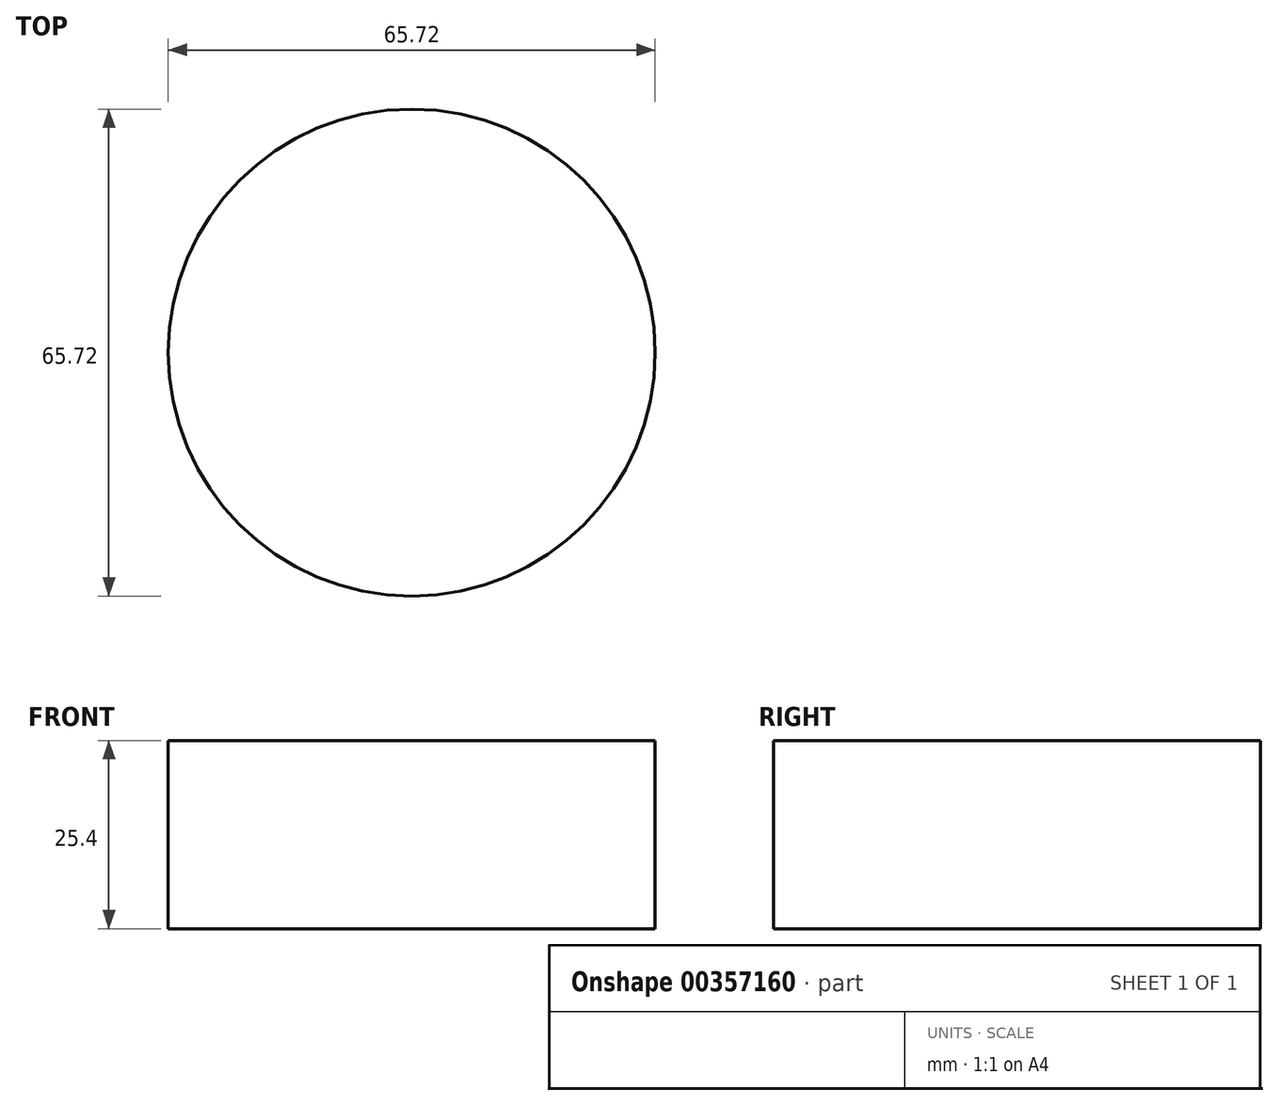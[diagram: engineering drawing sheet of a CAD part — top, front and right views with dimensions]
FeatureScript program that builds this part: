
annotation { "Feature Type Name" : "Feature", "Feature Type Description" : "" }
export const myFeature = defineFeature(function(context is Context, id is Id, definition is map)
    precondition{}
    {
        {
            var Q0;
            Q0=qCreatedBy(makeId("Top.planeOp"),FACE);
            var sketch = newSketch(context, id + "F0", { "sketchPlane" : qUnion([Q0])});
            skCircle(sketch, "E0", {"center": v(0, 0) * mm, "radius": 32.86 * mm});
            skSolve(sketch);
        }
        {
            var Q0;
            Q0 = qSketchRegion(id + "F0", true);
            extrude(context, id + "F1", {"entities" : qUnion([Q0]), "depth" : 25.4 * mm, "offsetDistance" : 25.4 * mm});
        }
    });
